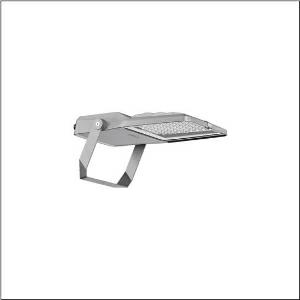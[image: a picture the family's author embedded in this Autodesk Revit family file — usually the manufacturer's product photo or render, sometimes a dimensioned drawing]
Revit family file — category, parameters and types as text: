
# Revit family: floodlight_fl_21_iq_mini___pl52_5xa7772c2d1a_8042
name_source: partatom
category: Lighting Fixtures
units: mm (PartAtom-declared; Revit-internal decimal feet)

## family parameters
Cut with Voids When Loaded = No
Host = Face
Light Source = No
Part Type = Normal
Room Calculation Point = No
Round Connector Dimension = Use Diameter
Shared = No

## types (1)
- --- (1 x LED, 12210 lm, 87.2 W, 3000K)
    Apparent Load = 87 VA
    CIE Flux Codes = 26 60 98 100 100
    Color Rendering = 70
    Color Temperature = 3000K
    Default Elevation = 1800 mm
    Description = Floodlight FL 21 iQ mini, floodlight, primary light control with lens, of PMMA, primary optical cover: protective disc, of toughened safety glass, transparent, light distribution: PL52, light emission: direct distribution, installation type: surface-mounted, lamps: LED, High Power LED, rated values: 12.210lm | 87,2W | 140lm/W (begin service life); end service life: 12.210lm | 92,1W; at 50% lumin. flux: 6.105lm | 40,1W | 152,2lm/W, colour temperature: 3000K, colour rendering: CRI > 70, light colour: 730, light setting 1 begin service life: 100% | 12.210lm | 87,2W | 140lm/W | 3.000K, light setting 1 end service life: 92,1W, further light settings possible, control: Street-Remote, Auto-Match, Temp-Guard, Night-Set, Smart-Wire, Desk-Remote (wireless, voltage-free reading and setting of iQ features in the workshop via application-optimized NFC function/RFID function), optimised constant luminous flux control (CLO 2.0), pre-setting: linear dimming characteristic, with terminal, 6-pole, mains connection: 220..240V, AC, 50/60Hz, luminaire housing, of diecast aluminium, powder-coated, SITECO metallic grey (DB 702S), corrosivity category C5 mid according to DIN EN ISO 12944suitable for swimming poolschlorine-resistant, sealing non-destructively replaceable, mounting bracket, of steel, galvanised, powder-coated, SITECO metallic grey (DB 702S), protection rating (complete): IP66, insulation class (complete): insulation class II (safety insulation), certification: CE, ENEC, VDE, protection symbol: D, impact resistance: IK08, permissible operating ambient temperature: -40..+40°C, permissible operating ambient temperature for outdoor applications: -40..+50°C, standard: DIN EN 12944, LABS conformity tested according to VDMA 24364:2018-05, packaging unit: 1 piece

Light Distribution: PL52
    Height = 70 mm
    Lamp = 1 x LED
    Lamp Light Flux = 12210 lm
    Lamp Power = 87.2 W
    Lamp count = 1
    Length = 485 mm
    Luminous efficacy = 140 lm/W
    Manufacturer = Siteco
    ModVariant = No
    Model = 5XA7772C2D1A
    Number of Poles = 1
    OnlyDefault = Yes
    Power Factor = 1
    Product Name = Floodlight FL 21 iQ mini | PL52
    Product group = floodlight | pylon annexe
    ProductGroupID = 6201
    Protection Class = Protection class II
    Protection Degree = IP 66
    RLX_Detail_Level = 1
    RLX_Emergency_Light_Flux = 0 lm
    RLX_Emergency_Type = 0
    RLX_Emergency_Type_DB = No
    RlxData = <blob elided: 96593 chars, md5=5dbe4d1d>
    Socket = socket
    Standby Power = 0 W
    System Light Flux = 12210 lm
    System Power = 87 W
    Type Comments = factory setting: luminous flux: 100 % | dim-lin: 254 | 456 mA
    Type Image = l_1006845.jpg
    URL = http://relux.com
    VarID = @adj_163845
    Voltage = 0 V
    Weight = 0.00 kg
    Width = 337 mm

## geometry (parser evidence)
native form markers: Blend x4, Sweep x12
no freeform markers — native parametric forms only
